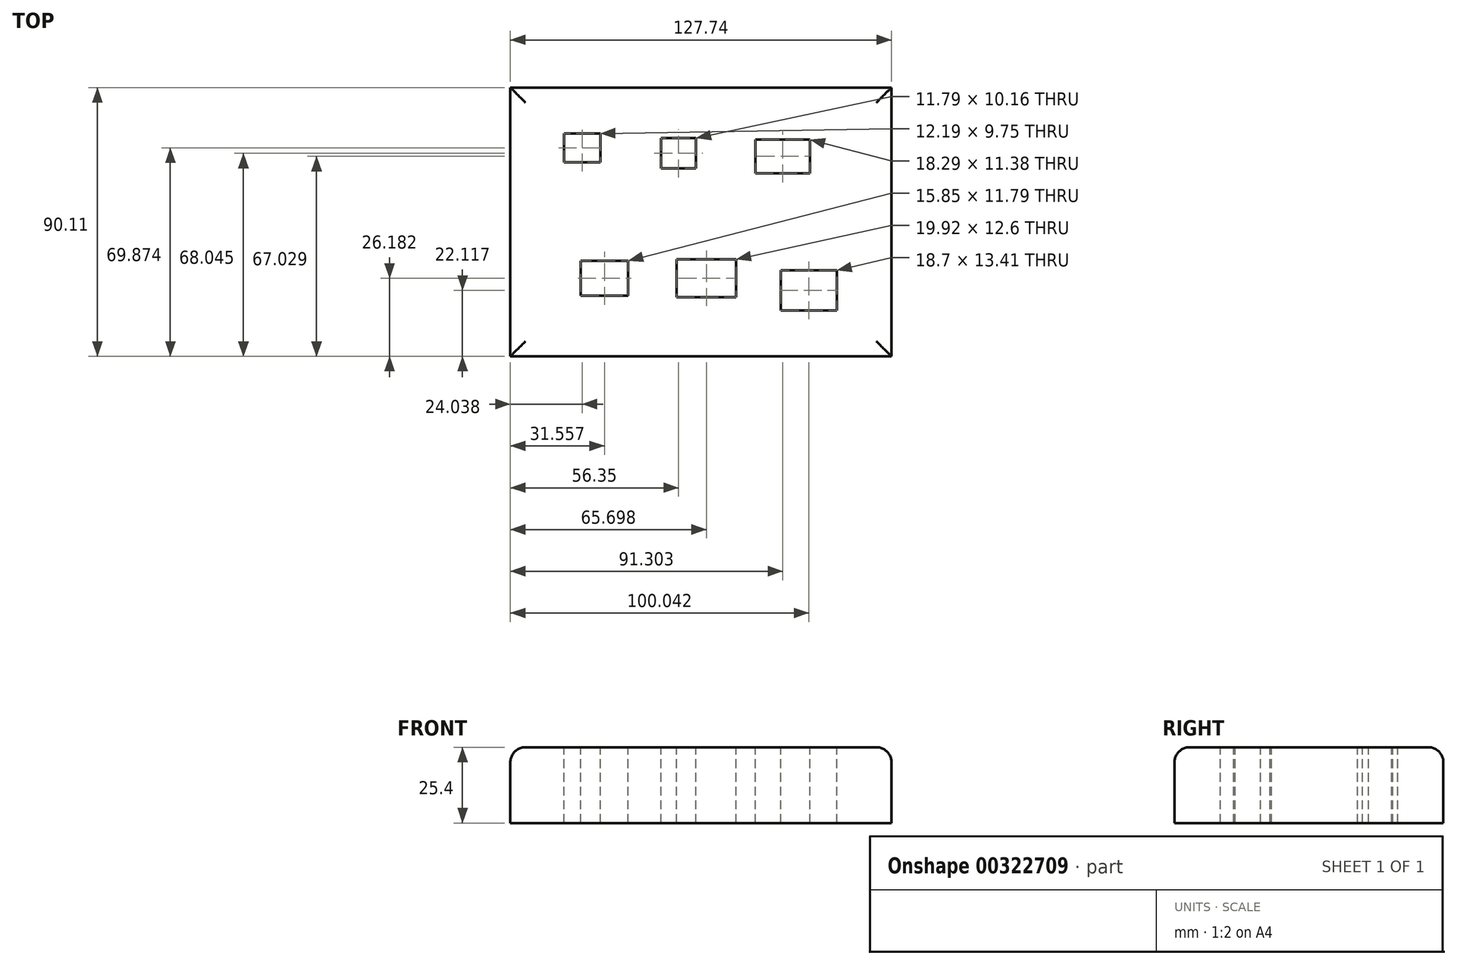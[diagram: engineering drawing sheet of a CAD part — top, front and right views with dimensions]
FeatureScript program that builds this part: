
annotation { "Feature Type Name" : "Feature", "Feature Type Description" : "" }
export const myFeature = defineFeature(function(context is Context, id is Id, definition is map)
    precondition{}
    {
        {
            var Q0;
            Q0=qCreatedBy(makeId("Top.planeOp"),FACE);
            var sketch = newSketch(context, id + "F0", { "sketchPlane" : qUnion([Q0])});
            skLineSegment(sketch, "E0.bottom", {"start": v(-55.74, 37.5) * mm, "end": v(72, 37.5) * mm});
            skLineSegment(sketch, "E0.top", {"start": v(-55.74, -52.6) * mm, "end": v(72, -52.6) * mm});
            skLineSegment(sketch, "E0.left", {"start": v(-55.74, 37.5) * mm, "end": v(-55.74, -52.6) * mm});
            skLineSegment(sketch, "E0.right", {"start": v(72, 37.5) * mm, "end": v(72, -52.6) * mm});
            skSolve(sketch);
        }
        {
            var Q0;
            Q0=makeQuery(id+"F0.imprint","IMPRINT",FACE,{"disambiguationData":[TD([[makeQuery(id+"F0.imprint","IMPRINT",EDGE,{"derivedFrom":sQuery(id+"F0.wireOp",EDGE,"E0.bottom")}),-1.0]])]});
            extrude(context, id + "F1", {"entities" : qUnion([Q0]), "depth" : 25.4 * mm});
        }
        {
            var Q0;
            Q0=makeQuery(id+"F1.opExtrude","CAP_FACE",FACE,{"disambiguationData":[OSD([sQuery(id+"F0.wireOp",EDGE,"E0.bottom"),sQuery(id+"F0.wireOp",EDGE,"E0.top"),sQuery(id+"F0.wireOp",EDGE,"E0.left"),sQuery(id+"F0.wireOp",EDGE,"E0.right")])],"isStart":false});
            var sketch = newSketch(context, id + "F2", { "sketchPlane" : qUnion([Q0])});
            skLineSegment(sketch, "E1.bottom", {"start": v(-37.8, 22.15) * mm, "end": v(-25.6, 22.15) * mm});
            skLineSegment(sketch, "E1.top", {"start": v(-37.8, 12.4) * mm, "end": v(-25.6, 12.4) * mm});
            skLineSegment(sketch, "E1.left", {"start": v(-37.8, 22.15) * mm, "end": v(-37.8, 12.4) * mm});
            skLineSegment(sketch, "E1.right", {"start": v(-25.6, 22.15) * mm, "end": v(-25.6, 12.4) * mm});
            skLineSegment(sketch, "E2.bottom", {"start": v(-5.28, 20.53) * mm, "end": v(6.5, 20.53) * mm});
            skLineSegment(sketch, "E2.top", {"start": v(-5.28, 10.36) * mm, "end": v(6.5, 10.36) * mm});
            skLineSegment(sketch, "E2.left", {"start": v(-5.28, 20.53) * mm, "end": v(-5.28, 10.36) * mm});
            skLineSegment(sketch, "E2.right", {"start": v(6.5, 20.53) * mm, "end": v(6.5, 10.36) * mm});
            skLineSegment(sketch, "E3.bottom", {"start": v(26.42, 20.12) * mm, "end": v(44.7, 20.12) * mm});
            skLineSegment(sketch, "E3.top", {"start": v(26.42, 8.74) * mm, "end": v(44.7, 8.74) * mm});
            skLineSegment(sketch, "E3.left", {"start": v(26.42, 20.12) * mm, "end": v(26.42, 8.74) * mm});
            skLineSegment(sketch, "E3.right", {"start": v(44.7, 20.12) * mm, "end": v(44.7, 8.74) * mm});
            skLineSegment(sketch, "E4.bottom", {"start": v(-32.1, -20.53) * mm, "end": v(-16.26, -20.53) * mm});
            skLineSegment(sketch, "E4.top", {"start": v(-32.1, -32.31) * mm, "end": v(-16.26, -32.31) * mm});
            skLineSegment(sketch, "E4.left", {"start": v(-32.1, -20.53) * mm, "end": v(-32.1, -32.31) * mm});
            skLineSegment(sketch, "E4.right", {"start": v(-16.26, -20.53) * mm, "end": v(-16.26, -32.31) * mm});
            skLineSegment(sketch, "E5.bottom", {"start": v(0, -20.12) * mm, "end": v(19.92, -20.12) * mm});
            skLineSegment(sketch, "E5.top", {"start": v(0, -32.72) * mm, "end": v(19.92, -32.72) * mm});
            skLineSegment(sketch, "E5.left", {"start": v(0, -20.12) * mm, "end": v(0, -32.72) * mm});
            skLineSegment(sketch, "E5.right", {"start": v(19.92, -20.12) * mm, "end": v(19.92, -32.72) * mm});
            skLineSegment(sketch, "E6.bottom", {"start": v(34.95, -23.78) * mm, "end": v(53.65, -23.78) * mm});
            skLineSegment(sketch, "E6.top", {"start": v(34.95, -37.19) * mm, "end": v(53.65, -37.19) * mm});
            skLineSegment(sketch, "E6.left", {"start": v(34.95, -23.78) * mm, "end": v(34.95, -37.19) * mm});
            skLineSegment(sketch, "E6.right", {"start": v(53.65, -23.78) * mm, "end": v(53.65, -37.19) * mm});
            skSolve(sketch);
        }
        {
            var Q0;
            Q0=makeQuery(id+"F2.imprint","IMPRINT",FACE,{"disambiguationData":[TD([[makeQuery(id+"F2.imprint","IMPRINT",EDGE,{"derivedFrom":sQuery(id+"F2.wireOp",EDGE,"E2.bottom")}),-1.0]])]});
            var Q1;
            Q1=makeQuery(id+"F2.imprint","IMPRINT",FACE,{"disambiguationData":[TD([[makeQuery(id+"F2.imprint","IMPRINT",EDGE,{"derivedFrom":sQuery(id+"F2.wireOp",EDGE,"E3.bottom")}),-1.0]])]});
            var Q2;
            Q2=makeQuery(id+"F2.imprint","IMPRINT",FACE,{"disambiguationData":[TD([[makeQuery(id+"F2.imprint","IMPRINT",EDGE,{"derivedFrom":sQuery(id+"F2.wireOp",EDGE,"E4.bottom")}),-1.0]])]});
            var Q3;
            Q3=makeQuery(id+"F2.imprint","IMPRINT",FACE,{"disambiguationData":[TD([[makeQuery(id+"F2.imprint","IMPRINT",EDGE,{"derivedFrom":sQuery(id+"F2.wireOp",EDGE,"E5.bottom")}),-1.0]])]});
            var Q4;
            Q4=makeQuery(id+"F2.imprint","IMPRINT",FACE,{"disambiguationData":[TD([[makeQuery(id+"F2.imprint","IMPRINT",EDGE,{"derivedFrom":sQuery(id+"F2.wireOp",EDGE,"E6.bottom")}),-1.0]])]});
            var Q5;
            Q5=makeQuery(id+"F2.imprint","IMPRINT",FACE,{"disambiguationData":[TD([[makeQuery(id+"F2.imprint","IMPRINT",EDGE,{"derivedFrom":sQuery(id+"F2.wireOp",EDGE,"E1.bottom")}),-1.0]])]});
            extrude(context, id + "F3", {"entities" : qUnion([Q0, Q1, Q2, Q3, Q4, Q5]), "operationType" : NewBodyOperationType.REMOVE, "oppositeDirection" : true, "depth" : 25.4 * mm});
        }
        {
            var Q0;
            Q0=makeQuery(id+"F3.boolean.opBoolean","COPY",EDGE,{"derivedFrom":makeQuery(id+"F3.opExtrude","CAP_EDGE",EDGE,{"disambiguationData":[OSD([sQuery(id+"F2.wireOp",EDGE,"E1.bottom")])],"isStart":true})});
            var Q1;
            Q1=makeQuery(id+"F3.boolean.opBoolean","COPY",EDGE,{"derivedFrom":makeQuery(id+"F3.opExtrude","CAP_EDGE",EDGE,{"disambiguationData":[OSD([sQuery(id+"F2.wireOp",EDGE,"E1.left")])],"isStart":true})});
            var Q2;
            Q2=makeQuery(id+"F3.boolean.opBoolean","COPY",EDGE,{"derivedFrom":makeQuery(id+"F3.opExtrude","CAP_EDGE",EDGE,{"disambiguationData":[OSD([sQuery(id+"F2.wireOp",EDGE,"E1.top")])],"isStart":true})});
            var Q3;
            Q3=makeQuery(id+"F3.boolean.opBoolean","COPY",EDGE,{"derivedFrom":makeQuery(id+"F3.opExtrude","CAP_EDGE",EDGE,{"disambiguationData":[OSD([sQuery(id+"F2.wireOp",EDGE,"E1.right")])],"isStart":true})});
            var Q4;
            Q4=makeQuery(id+"F3.boolean.opBoolean","COPY",EDGE,{"derivedFrom":makeQuery(id+"F3.opExtrude","CAP_EDGE",EDGE,{"disambiguationData":[OSD([sQuery(id+"F2.wireOp",EDGE,"E2.bottom")])],"isStart":true})});
            var Q5;
            Q5=makeQuery(id+"F3.boolean.opBoolean","COPY",EDGE,{"derivedFrom":makeQuery(id+"F3.opExtrude","CAP_EDGE",EDGE,{"disambiguationData":[OSD([sQuery(id+"F2.wireOp",EDGE,"E2.right")])],"isStart":true})});
            var Q6;
            Q6=makeQuery(id+"F3.boolean.opBoolean","COPY",EDGE,{"derivedFrom":makeQuery(id+"F3.opExtrude","CAP_EDGE",EDGE,{"disambiguationData":[OSD([sQuery(id+"F2.wireOp",EDGE,"E2.top")])],"isStart":true})});
            var Q7;
            Q7=makeQuery(id+"F3.boolean.opBoolean","COPY",EDGE,{"derivedFrom":makeQuery(id+"F3.opExtrude","CAP_EDGE",EDGE,{"disambiguationData":[OSD([sQuery(id+"F2.wireOp",EDGE,"E2.left")])],"isStart":true})});
            var Q8;
            Q8=makeQuery(id+"F3.boolean.opBoolean","COPY",EDGE,{"derivedFrom":makeQuery(id+"F3.opExtrude","CAP_EDGE",EDGE,{"disambiguationData":[OSD([sQuery(id+"F2.wireOp",EDGE,"E3.bottom")])],"isStart":true})});
            var Q9;
            Q9=makeQuery(id+"F3.boolean.opBoolean","COPY",EDGE,{"derivedFrom":makeQuery(id+"F3.opExtrude","CAP_EDGE",EDGE,{"disambiguationData":[OSD([sQuery(id+"F2.wireOp",EDGE,"E3.top")])],"isStart":true})});
            var Q10;
            Q10=makeQuery(id+"F3.boolean.opBoolean","COPY",EDGE,{"derivedFrom":makeQuery(id+"F3.opExtrude","CAP_EDGE",EDGE,{"disambiguationData":[OSD([sQuery(id+"F2.wireOp",EDGE,"E3.left")])],"isStart":true})});
            var Q11;
            Q11=makeQuery(id+"F3.boolean.opBoolean","COPY",EDGE,{"derivedFrom":makeQuery(id+"F3.opExtrude","CAP_EDGE",EDGE,{"disambiguationData":[OSD([sQuery(id+"F2.wireOp",EDGE,"E3.right")])],"isStart":true})});
            var Q12;
            Q12=makeQuery(id+"F3.boolean.opBoolean","COPY",EDGE,{"derivedFrom":makeQuery(id+"F3.opExtrude","CAP_EDGE",EDGE,{"disambiguationData":[OSD([sQuery(id+"F2.wireOp",EDGE,"E5.right")])],"isStart":true})});
            var Q13;
            Q13=makeQuery(id+"F3.boolean.opBoolean","COPY",EDGE,{"derivedFrom":makeQuery(id+"F3.opExtrude","CAP_EDGE",EDGE,{"disambiguationData":[OSD([sQuery(id+"F2.wireOp",EDGE,"E5.top")])],"isStart":true})});
            var Q14;
            Q14=makeQuery(id+"F3.boolean.opBoolean","COPY",EDGE,{"derivedFrom":makeQuery(id+"F3.opExtrude","CAP_EDGE",EDGE,{"disambiguationData":[OSD([sQuery(id+"F2.wireOp",EDGE,"E5.left")])],"isStart":true})});
            var Q15;
            Q15=makeQuery(id+"F3.boolean.opBoolean","COPY",EDGE,{"derivedFrom":makeQuery(id+"F3.opExtrude","CAP_EDGE",EDGE,{"disambiguationData":[OSD([sQuery(id+"F2.wireOp",EDGE,"E5.bottom")])],"isStart":true})});
            var Q16;
            Q16=makeQuery(id+"F3.boolean.opBoolean","COPY",EDGE,{"derivedFrom":makeQuery(id+"F3.opExtrude","CAP_EDGE",EDGE,{"disambiguationData":[OSD([sQuery(id+"F2.wireOp",EDGE,"E6.left")])],"isStart":true})});
            var Q17;
            Q17=makeQuery(id+"F3.boolean.opBoolean","COPY",EDGE,{"derivedFrom":makeQuery(id+"F3.opExtrude","CAP_EDGE",EDGE,{"disambiguationData":[OSD([sQuery(id+"F2.wireOp",EDGE,"E6.bottom")])],"isStart":true})});
            var Q18;
            Q18=makeQuery(id+"F3.boolean.opBoolean","COPY",EDGE,{"derivedFrom":makeQuery(id+"F3.opExtrude","CAP_EDGE",EDGE,{"disambiguationData":[OSD([sQuery(id+"F2.wireOp",EDGE,"E6.right")])],"isStart":true})});
            var Q19;
            Q19=makeQuery(id+"F3.boolean.opBoolean","COPY",EDGE,{"derivedFrom":makeQuery(id+"F3.opExtrude","CAP_EDGE",EDGE,{"disambiguationData":[OSD([sQuery(id+"F2.wireOp",EDGE,"E6.top")])],"isStart":true})});
            var Q20;
            Q20=makeQuery(id+"F3.boolean.opBoolean","COPY",EDGE,{"derivedFrom":makeQuery(id+"F3.opExtrude","CAP_EDGE",EDGE,{"disambiguationData":[OSD([sQuery(id+"F2.wireOp",EDGE,"E4.left")])],"isStart":true})});
            var Q21;
            Q21=makeQuery(id+"F3.boolean.opBoolean","COPY",EDGE,{"derivedFrom":makeQuery(id+"F3.opExtrude","CAP_EDGE",EDGE,{"disambiguationData":[OSD([sQuery(id+"F2.wireOp",EDGE,"E4.bottom")])],"isStart":true})});
            var Q22;
            Q22=makeQuery(id+"F3.boolean.opBoolean","COPY",EDGE,{"derivedFrom":makeQuery(id+"F3.opExtrude","CAP_EDGE",EDGE,{"disambiguationData":[OSD([sQuery(id+"F2.wireOp",EDGE,"E4.top")])],"isStart":true})});
            var Q23;
            Q23=makeQuery(id+"F3.boolean.opBoolean","COPY",EDGE,{"derivedFrom":makeQuery(id+"F3.opExtrude","CAP_EDGE",EDGE,{"disambiguationData":[OSD([sQuery(id+"F2.wireOp",EDGE,"E4.right")])],"isStart":true})});
            var Q24;
            Q24=makeQuery(id+"F1.opExtrude","CAP_EDGE",EDGE,{"disambiguationData":[OSD([sQuery(id+"F0.wireOp",EDGE,"E0.bottom")])],"isStart":false});
            var Q25;
            Q25=makeQuery(id+"F1.opExtrude","CAP_EDGE",EDGE,{"disambiguationData":[OSD([sQuery(id+"F0.wireOp",EDGE,"E0.right")])],"isStart":false});
            var Q26;
            Q26=makeQuery(id+"F1.opExtrude","CAP_EDGE",EDGE,{"disambiguationData":[OSD([sQuery(id+"F0.wireOp",EDGE,"E0.top")])],"isStart":false});
            var Q27;
            Q27=makeQuery(id+"F1.opExtrude","CAP_EDGE",EDGE,{"disambiguationData":[OSD([sQuery(id+"F0.wireOp",EDGE,"E0.left")])],"isStart":false});
            fillet(context, id + "F4", {"entities" : qUnion([Q0, Q1, Q2, Q3, Q4, Q5, Q6, Q7, Q8, Q9, Q10, Q11, Q12, Q13, Q14, Q15, Q16, Q17, Q18, Q19, Q20, Q21, Q22, Q23, Q24, Q25, Q26, Q27]), "radius" : 5.08 * mm, "tangentPropagation" : true, "allowEdgeOverflow" : false});
        }
    });
